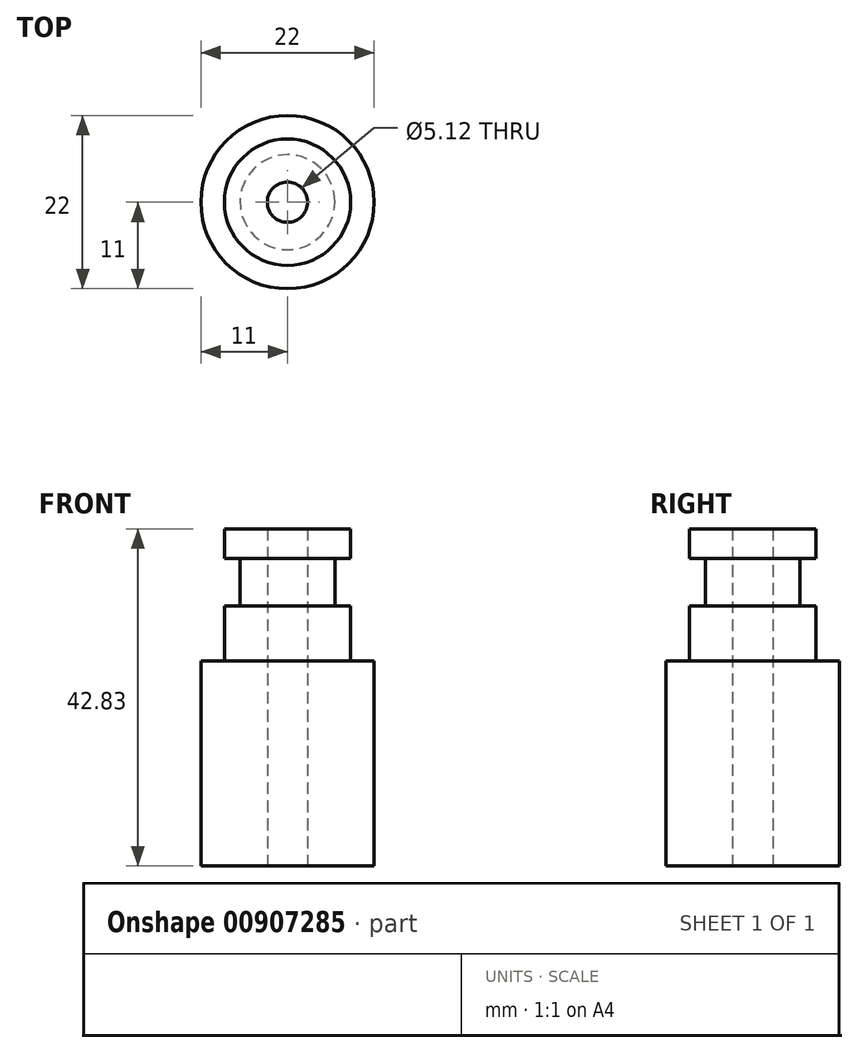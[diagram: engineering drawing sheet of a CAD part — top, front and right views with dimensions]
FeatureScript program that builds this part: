
annotation { "Feature Type Name" : "Feature", "Feature Type Description" : "" }
export const myFeature = defineFeature(function(context is Context, id is Id, definition is map)
    precondition{}
    {
        {
            var Q0;
            Q0=qCreatedBy(makeId("Top.planeOp"),FACE);
            var sketch = newSketch(context, id + "F0", { "sketchPlane" : qUnion([Q0])});
            skCircle(sketch, "E0", {"center": v(0, 0) * mm, "radius": 11 * mm});
            skCircle(sketch, "E1", {"center": v(0, 0) * mm, "radius": 6.03 * mm});
            skCircle(sketch, "E2", {"center": v(0, 0) * mm, "radius": 8.03 * mm});
            skSolve(sketch);
        }
        {
            var Q0;
            Q0=makeQuery(id+"F0.imprint","IMPRINT",FACE,{"disambiguationData":[TD([[makeQuery(id+"F0.imprint","IMPRINT",EDGE,{"derivedFrom":sQuery(id+"F0.wireOp",EDGE,"E0")}),1.0]])]});
            var Q1;
            Q1=makeQuery(id+"F0.imprint","IMPRINT",FACE,{"disambiguationData":[TD([[makeQuery(id+"F0.imprint","IMPRINT",EDGE,{"derivedFrom":sQuery(id+"F0.wireOp",EDGE,"E1")}),1.0]])]});
            var Q2;
            Q2=makeQuery(id+"F0.imprint","IMPRINT",FACE,{"disambiguationData":[TD([[makeQuery(id+"F0.imprint","IMPRINT",EDGE,{"derivedFrom":sQuery(id+"F0.wireOp",EDGE,"E1")}),-1.0]])]});
            extrude(context, id + "F1", {"entities" : qUnion([Q0, Q1, Q2]), "oppositeDirection" : true, "depth" : 26.05 * mm, "offsetDistance" : 25 * mm});
        }
        {
            var Q0;
            Q0=makeQuery(id+"F0.imprint","IMPRINT",FACE,{"disambiguationData":[TD([[makeQuery(id+"F0.imprint","IMPRINT",EDGE,{"derivedFrom":sQuery(id+"F0.wireOp",EDGE,"E1")}),1.0]])]});
            var Q1;
            Q1=makeQuery(id+"F0.imprint","IMPRINT",FACE,{"disambiguationData":[TD([[makeQuery(id+"F0.imprint","IMPRINT",EDGE,{"derivedFrom":sQuery(id+"F0.wireOp",EDGE,"E1")}),-1.0]])]});
            extrude(context, id + "F2", {"entities" : qUnion([Q0, Q1]), "operationType" : NewBodyOperationType.ADD, "depth" : 16.78 * mm, "offsetDistance" : 25 * mm});
        }
        {
            var Q0;
            Q0=makeQuery(id+"F0.imprint","IMPRINT",FACE,{"disambiguationData":[TD([[makeQuery(id+"F0.imprint","IMPRINT",EDGE,{"derivedFrom":sQuery(id+"F0.wireOp",EDGE,"E1")}),-1.0]])]});
            extrude(context, id + "F3", {"entities" : qUnion([Q0]), "operationType" : NewBodyOperationType.REMOVE, "depth" : 13 * mm, "offsetDistance" : 25 * mm});
        }
        {
            var Q0;
            Q0=makeQuery(id+"F0.imprint","IMPRINT",FACE,{"disambiguationData":[TD([[makeQuery(id+"F0.imprint","IMPRINT",EDGE,{"derivedFrom":sQuery(id+"F0.wireOp",EDGE,"E1")}),-1.0]])]});
            extrude(context, id + "F4", {"entities" : qUnion([Q0]), "operationType" : NewBodyOperationType.ADD, "depth" : 7 * mm, "offsetDistance" : 25 * mm});
        }
        {
            var Q0;
            Q0=makeQuery(id+"F1.opExtrude","CAP_FACE",FACE,{"disambiguationData":[OSD([sQuery(id+"F0.wireOp",EDGE,"E0")])],"isStart":false});
            var sketch = newSketch(context, id + "F5", { "sketchPlane" : qUnion([Q0])});
            skPoint(sketch, "E3.0", {"position": v(0, 0) * mm});
            skSolve(sketch);
        }
        {
            var Q0;
            Q0=sQuery(id+"F5.wireOp",VERTEX,"E3.0");
            var Q1;
            Q1=makeQuery(id+"F1.opExtrude","SWEPT_BODY",BODY,{"disambiguationData":[OSD([sQuery(id+"F0.wireOp",EDGE,"E0")])]});
            hole(context, id + "F6", {"style" : HoleStyle.SIMPLE, "endStyle" : HoleEndStyle.BLIND, "holeDiameter" : 5.12 * mm, "majorDiameter" : 5 * mm, "holeDepth" : 120 * mm, "isTappedThrough" : true, "tappedDepth" : 12 * mm, "tapClearance" : 3, "locations" : qUnion([Q0]), "scope" : qUnion([Q1])});
        }
    });
